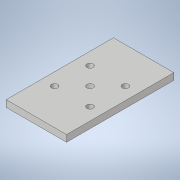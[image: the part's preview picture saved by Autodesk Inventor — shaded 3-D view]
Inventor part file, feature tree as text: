
AUTODESK INVENTOR PART (.ipt)
format: ipt  version: 2022 (Build 260153000, 153)  size: 124,928 bytes
history: native  units: in
note: dims shown in document units (in); Inventor stores cm internally (conversion verified against a paired STEP export)
features: sketch x3, extrude x2, hole x1
ambient origin geometry x8: Origin, YZ Plane, XZ Plane, XY Plane, X Axis, Y Axis, Z Axis, Center Point
bodies: Solid1 (feature_tree)
feature tree (6):
  extrude  "Extrusion1"  Depth=1.13in
  hole  "Hole1"  [1 undecoded]
  extrude  "Extrusion2"  Depth=0.7874in
  sketch  "Sketch1"  dims[d0=2.0079in d1=1.13in]
  sketch  "Sketch2"  dims[d2=0.125in d3=0.0in d4=0.118in]
  sketch  "Sketch3"  dims[d5=0.3315in d6=0.7874in d8=0.663in d9=0.7874in d11=0.663in d14=0.3315in d15=0.118in d16=0.18in d17=0.375in d18=0.25in d19=0.5635in d20=0.22in d21=0.8108in d22=0.118in d23=0.25in d24=0.0in]
note: 1 required parameter value undecoded (feature->parameter linkage not recoverable at this tier; creation-order binding heuristic only, values carry confidence <= 0.55)
